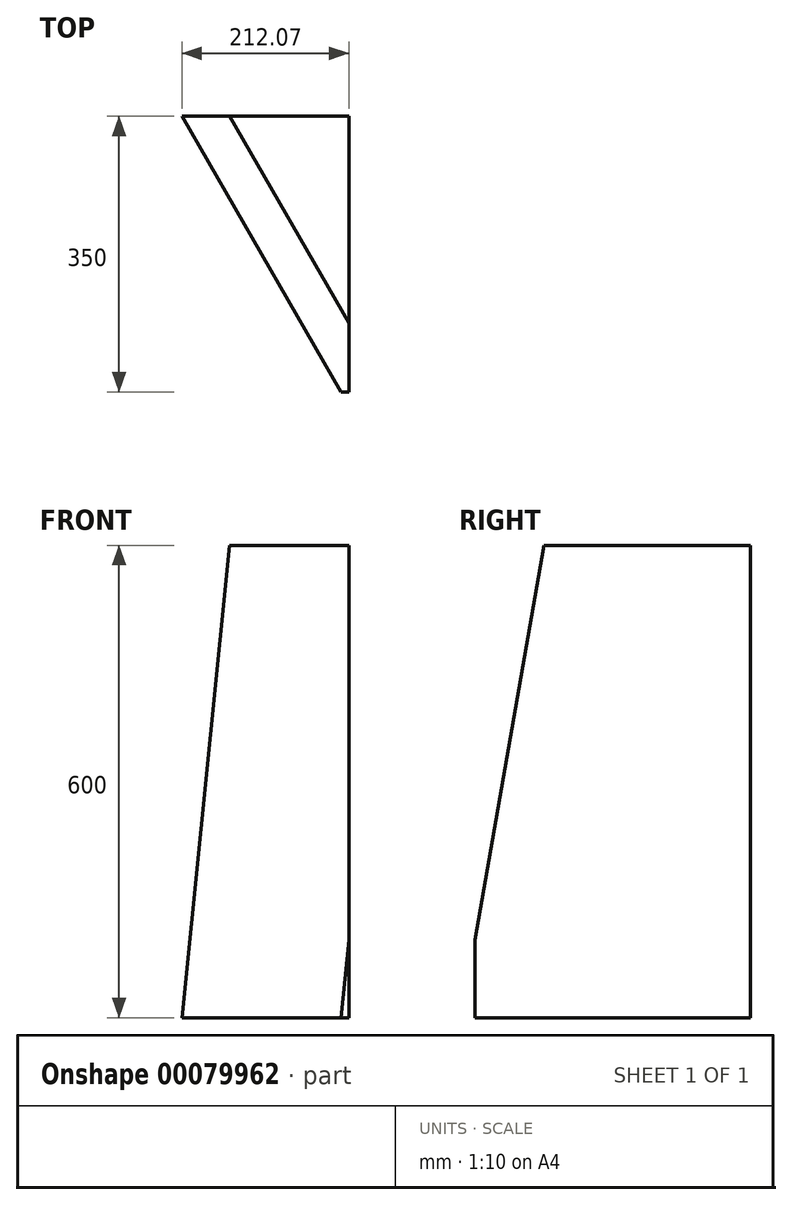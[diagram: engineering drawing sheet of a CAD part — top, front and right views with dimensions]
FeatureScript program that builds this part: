
annotation { "Feature Type Name" : "Feature", "Feature Type Description" : "" }
export const myFeature = defineFeature(function(context is Context, id is Id, definition is map)
    precondition{}
    {
        {
            var Q0;
            Q0=qCreatedBy(makeId("Top.planeOp"),FACE);
            var sketch = newSketch(context, id + "F0", { "sketchPlane" : qUnion([Q0])});
            skLineSegment(sketch, "E0", {"start": v(0, 0) * mm, "end": v(-10, 0) * mm});
            skLineSegment(sketch, "E1", {"start": v(-10, 0) * mm, "end": v(-212.07, 350) * mm});
            skLineSegment(sketch, "E2", {"start": v(-212.07, 350) * mm, "end": v(0, 350) * mm});
            skLineSegment(sketch, "E3", {"start": v(0, 350) * mm, "end": v(0, 0) * mm});
            skSolve(sketch);
        }
        {
            var Q0;
            Q0 = qSketchRegion(id + "F0", true);
            extrude(context, id + "F1", {"entities" : qUnion([Q0]), "depth" : 600 * mm});
        }
        {
            var Q0;
            Q0=makeQuery(id+"F1.opExtrude","SWEPT_FACE",FACE,{"disambiguationData":[OSD([sQuery(id+"F0.wireOp",EDGE,"E2")])]});
            var Q1;
            Q1=makeQuery(id+"F1.opExtrude","SWEPT_EDGE",EDGE,{"disambiguationData":[OSD([sQuery(id+"F0.wireOp",EDGE,"E1"),sQuery(id+"F0.wireOp",EDGE,"E2")])]});
            cPlane(context, id + "F2", {"entities" : qUnion([Q0, Q1]), "cplaneType" : CPlaneType.LINE_ANGLE, "offset" : 150 * mm, "angle" : 150 * degree, "width" : 150 * mm, "height" : 150 * mm});
        }
        {
            var Q0;
            Q0=qCreatedBy(id+"F2.planeOp",FACE);
            var sketch = newSketch(context, id + "F3", { "sketchPlane" : qUnion([Q0])});
            skLineSegment(sketch, "E4", {"start": v(-43.83, 600) * mm, "end": v(8.66, 0) * mm});
            skLineSegment(sketch, "E5", {"start": v(8.66, 0) * mm, "end": v(8.66, 600) * mm});
            skLineSegment(sketch, "E6", {"start": v(8.66, 600) * mm, "end": v(-43.83, 600) * mm});
            skSolve(sketch);
        }
        {
            var Q0;
            Q0 = qSketchRegion(id + "F3", true);
            extrude(context, id + "F4", {"entities" : qUnion([Q0]), "operationType" : NewBodyOperationType.REMOVE, "endBound" : BoundingType.THROUGH_ALL, "oppositeDirection" : true, "depth" : 200 * mm});
        }
    });
